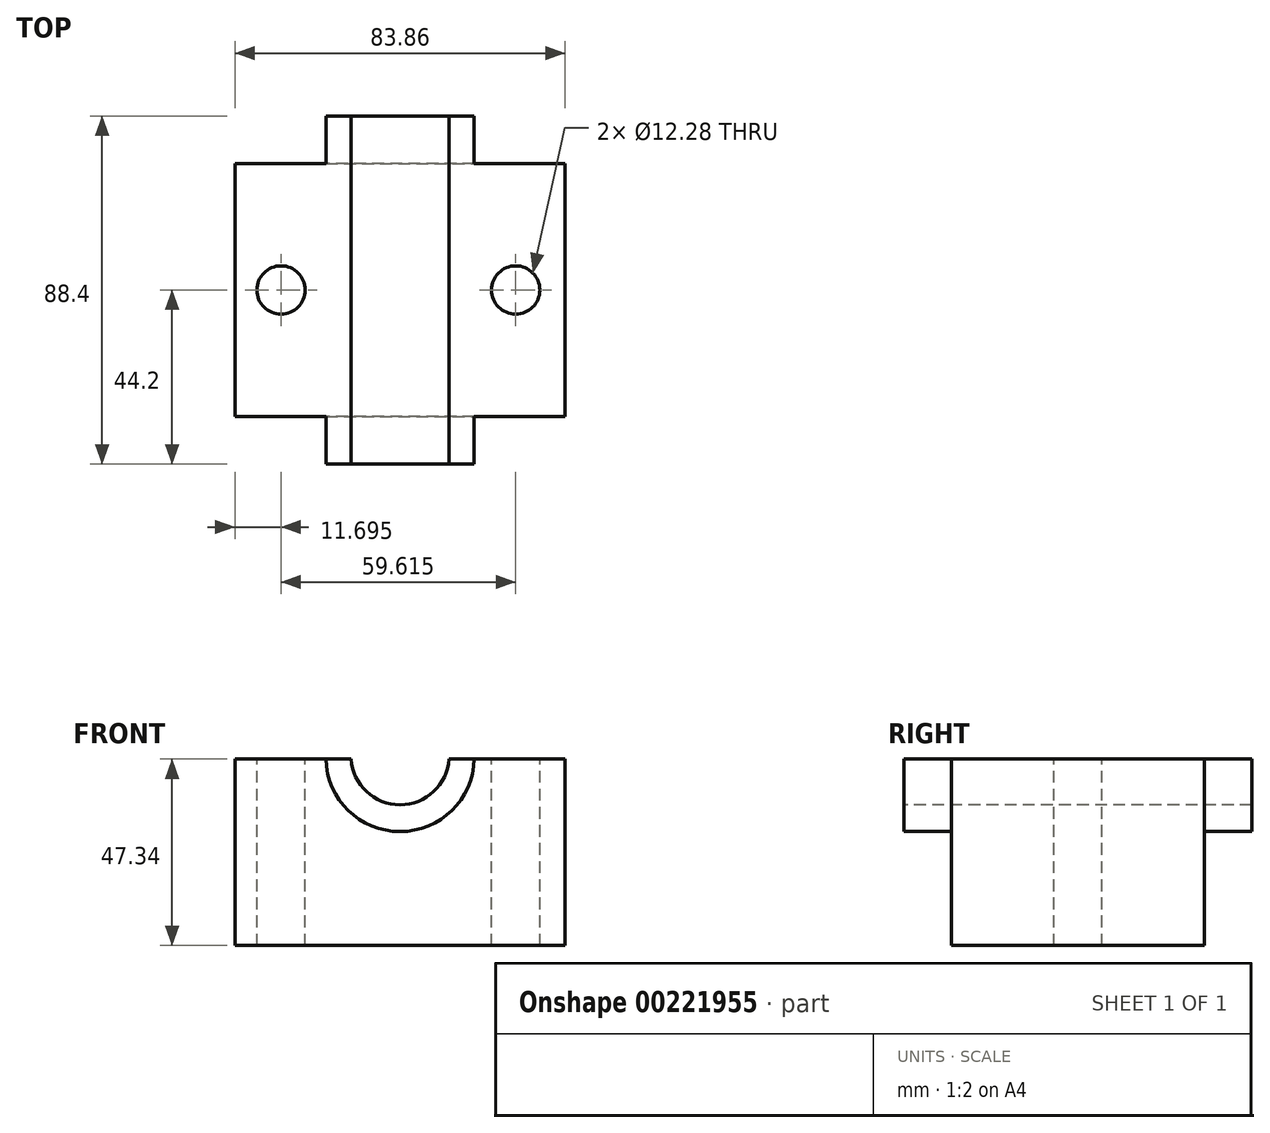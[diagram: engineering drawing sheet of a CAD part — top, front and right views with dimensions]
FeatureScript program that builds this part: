
annotation { "Feature Type Name" : "Feature", "Feature Type Description" : "" }
export const myFeature = defineFeature(function(context is Context, id is Id, definition is map)
    precondition{}
    {
        {
            var Q0;
            Q0=qCreatedBy(makeId("Top.planeOp"),FACE);
            var sketch = newSketch(context, id + "F0", { "sketchPlane" : qUnion([Q0])});
            skLineSegment(sketch, "E0.bottom", {"start": v(41.93, 32.09) * mm, "end": v(-41.93, 32.09) * mm});
            skLineSegment(sketch, "E0.top", {"start": v(41.93, -32.09) * mm, "end": v(-41.93, -32.09) * mm});
            skLineSegment(sketch, "E0.left", {"start": v(41.93, 32.09) * mm, "end": v(41.93, -32.09) * mm});
            skLineSegment(sketch, "E0.right", {"start": v(-41.93, 32.09) * mm, "end": v(-41.93, -32.09) * mm});
            skPoint(sketch, "E0.middle", {"position": v(0, 0) * mm});
            skSolve(sketch);
        }
        {
            var Q0;
            Q0 = qSketchRegion(id + "F0", true);
            extrude(context, id + "F1", {"entities" : qUnion([Q0]), "depth" : 48.26 * mm});
        }
        {
            var Q0;
            Q0=qCreatedBy(makeId("Front.planeOp"),FACE);
            var sketch = newSketch(context, id + "F2", { "sketchPlane" : qUnion([Q0])});
            skCircle(sketch, "E1", {"center": v(0, 47.78) * mm, "radius": 18.83 * mm});
            skSolve(sketch);
        }
        {
            var Q0;
            Q0 = qSketchRegion(id + "F2", true);
            extrude(context, id + "F3", {"entities" : qUnion([Q0]), "operationType" : NewBodyOperationType.ADD, "depth" : 44.2 * mm, "hasSecondDirection" : true, "secondDirectionOppositeDirection" : true, "secondDirectionDepth" : 44.2 * mm});
        }
        {
            var Q0;
            Q0=qCreatedBy(makeId("Front.planeOp"),FACE);
            var sketch = newSketch(context, id + "F4", { "sketchPlane" : qUnion([Q0])});
            skCircle(sketch, "E2", {"center": v(0, 48.28) * mm, "radius": 12.54 * mm});
            skSolve(sketch);
        }
        {
            var Q0;
            Q0 = qSketchRegion(id + "F4", true);
            extrude(context, id + "F5", {"entities" : qUnion([Q0]), "operationType" : NewBodyOperationType.REMOVE, "endBound" : BoundingType.THROUGH_ALL, "oppositeDirection" : true, "depth" : 25.4 * mm, "hasSecondDirection" : true, "secondDirectionBound" : SecondDirectionBoundingType.THROUGH_ALL, "secondDirectionOppositeDirection" : false, "secondDirectionDepth" : 25.4 * mm});
        }
        {
            var Q0;
            Q0=qCreatedBy(makeId("Front.planeOp"),FACE);
            var sketch = newSketch(context, id + "F6", { "sketchPlane" : qUnion([Q0])});
            skLineSegment(sketch, "E3", {"start": v(42.95, 47.34) * mm, "end": v(-43.34, 47.34) * mm});
            skLineSegment(sketch, "E4", {"start": v(-43.34, 47.34) * mm, "end": v(-43.34, 70.21) * mm});
            skLineSegment(sketch, "E5", {"start": v(-43.34, 70.21) * mm, "end": v(48.38, 70.21) * mm});
            skLineSegment(sketch, "E6", {"start": v(48.38, 70.21) * mm, "end": v(42.95, 47.34) * mm});
            skSolve(sketch);
        }
        {
            var Q0;
            Q0 = qSketchRegion(id + "F6", true);
            extrude(context, id + "F7", {"entities" : qUnion([Q0]), "operationType" : NewBodyOperationType.REMOVE, "endBound" : BoundingType.THROUGH_ALL, "oppositeDirection" : true, "depth" : 25.4 * mm, "hasSecondDirection" : true, "secondDirectionBound" : SecondDirectionBoundingType.THROUGH_ALL, "secondDirectionOppositeDirection" : false, "secondDirectionDepth" : 25.4 * mm});
        }
        {
            var Q0;
            Q0=qCreatedBy(makeId("Top.planeOp"),FACE);
            var sketch = newSketch(context, id + "F8", { "sketchPlane" : qUnion([Q0])});
            skCircle(sketch, "E7", {"center": v(-30.24, 0) * mm, "radius": 6.14 * mm});
            skCircle(sketch, "E8", {"center": v(29.38, 0) * mm, "radius": 6.14 * mm});
            skSolve(sketch);
        }
        {
            var Q0;
            Q0 = qSketchRegion(id + "F8", true);
            extrude(context, id + "F9", {"entities" : qUnion([Q0]), "operationType" : NewBodyOperationType.REMOVE, "endBound" : BoundingType.THROUGH_ALL, "oppositeDirection" : true, "depth" : 25.4 * mm, "hasSecondDirection" : true, "secondDirectionBound" : SecondDirectionBoundingType.THROUGH_ALL, "secondDirectionOppositeDirection" : false, "secondDirectionDepth" : 25.4 * mm});
        }
    });
